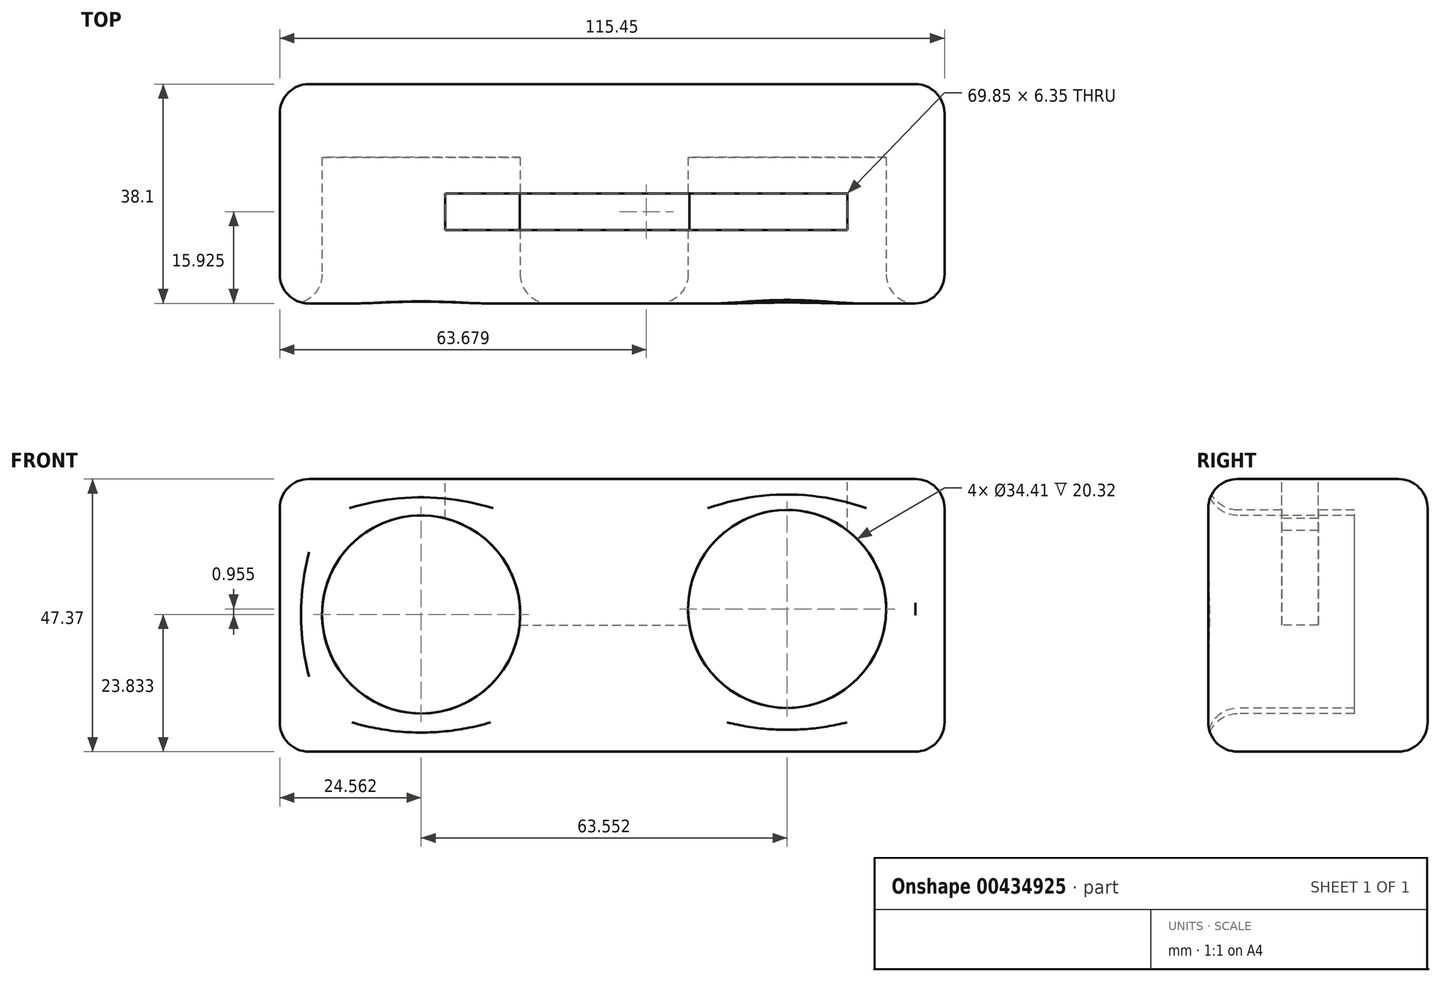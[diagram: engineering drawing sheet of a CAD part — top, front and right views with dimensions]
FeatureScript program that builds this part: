
annotation { "Feature Type Name" : "Feature", "Feature Type Description" : "" }
export const myFeature = defineFeature(function(context is Context, id is Id, definition is map)
    precondition{}
    {
        {
            var Q0;
            Q0=qCreatedBy(makeId("Front.planeOp"),FACE);
            var sketch = newSketch(context, id + "F0", { "sketchPlane" : qUnion([Q0])});
            skLineSegment(sketch, "E0.bottom", {"start": v(-65.78, 0) * mm, "end": v(68.72, 0) * mm});
            skLineSegment(sketch, "E0.top", {"start": v(-65.78, 47.37) * mm, "end": v(68.72, 47.37) * mm});
            skLineSegment(sketch, "E0.left", {"start": v(-65.78, 0) * mm, "end": v(-65.78, 47.37) * mm});
            skLineSegment(sketch, "E0.right", {"start": v(68.72, 0) * mm, "end": v(68.72, 47.37) * mm});
            skSolve(sketch);
        }
        {
            var Q0;
            Q0 = qSketchRegion(id + "F0", true);
            extrude(context, id + "F1", {"entities" : qUnion([Q0]), "depth" : 38.1 * mm});
        }
        {
            var Q0;
            Q0=makeQuery(id+"F1.opExtrude","CAP_FACE",FACE,{"disambiguationData":[OSD([sQuery(id+"F0.wireOp",EDGE,"E0.bottom"),sQuery(id+"F0.wireOp",EDGE,"E0.top"),sQuery(id+"F0.wireOp",EDGE,"E0.left"),sQuery(id+"F0.wireOp",EDGE,"E0.right")])],"isStart":false});
            var sketch = newSketch(context, id + "F2", { "sketchPlane" : qUnion([Q0])});
            skCircle(sketch, "E1", {"center": v(-41.22, 23.83) * mm, "radius": 17.2 * mm});
            skCircle(sketch, "E2", {"center": v(22.33, 24.79) * mm, "radius": 17.2 * mm});
            skSolve(sketch);
        }
        {
            var Q0;
            Q0 = qSketchRegion(id + "F2", true);
            extrude(context, id + "F3", {"entities" : qUnion([Q0]), "operationType" : NewBodyOperationType.REMOVE, "oppositeDirection" : true, "depth" : 25.4 * mm});
        }
        {
            var Q0;
            Q0=makeQuery(id+"F1.opExtrude","SWEPT_FACE",FACE,{"disambiguationData":[OSD([sQuery(id+"F0.wireOp",EDGE,"E0.top")])]});
            var sketch = newSketch(context, id + "F4", { "sketchPlane" : qUnion([Q0])});
            skLineSegment(sketch, "E3.bottom", {"start": v(-37.03, -19) * mm, "end": v(32.82, -19) * mm});
            skLineSegment(sketch, "E3.top", {"start": v(-37.03, -25.35) * mm, "end": v(32.82, -25.35) * mm});
            skLineSegment(sketch, "E3.left", {"start": v(-37.03, -19) * mm, "end": v(-37.03, -25.35) * mm});
            skLineSegment(sketch, "E3.right", {"start": v(32.82, -19) * mm, "end": v(32.82, -25.35) * mm});
            skSolve(sketch);
        }
        {
            var Q0;
            Q0=makeQuery(id+"F4.imprint","IMPRINT",FACE,{"disambiguationData":[TD([[makeQuery(id+"F4.imprint","IMPRINT",EDGE,{"derivedFrom":sQuery(id+"F4.wireOp",EDGE,"E3.bottom")}),-1.0]])]});
            extrude(context, id + "F5", {"entities" : qUnion([Q0]), "operationType" : NewBodyOperationType.REMOVE, "oppositeDirection" : true, "depth" : 25.4 * mm});
        }
        {
            var Q0;
            Q0=makeQuery(id+"F1.opExtrude","SWEPT_FACE",FACE,{"disambiguationData":[OSD([sQuery(id+"F0.wireOp",EDGE,"E0.right")])]});
            extrude(context, id + "F6", {"entities" : qUnion([Q0]), "operationType" : NewBodyOperationType.REMOVE, "oppositeDirection" : true, "depth" : 19.05 * mm});
        }
        {
            var Q0;
            Q0=makeQuery(id+"F1.opExtrude","CAP_EDGE",EDGE,{"disambiguationData":[OSD([sQuery(id+"F0.wireOp",EDGE,"E0.top")])],"isStart":false});
            var Q1;
            Q1=makeQuery(id+"F6.boolean.opBoolean","COPY",EDGE,{"derivedFrom":makeQuery(id+"F6.opExtrude","CAP_EDGE",EDGE,{"disambiguationData":[OSD([sQuery(id+"F0.wireOp",EDGE,"E0.top"),sQuery(id+"F0.wireOp",EDGE,"E0.right")])],"isStart":false})});
            var Q2;
            Q2=makeQuery(id+"F1.opExtrude","CAP_EDGE",EDGE,{"disambiguationData":[OSD([sQuery(id+"F0.wireOp",EDGE,"E0.top")])],"isStart":true});
            var Q3;
            Q3=makeQuery(id+"F1.opExtrude","SWEPT_EDGE",EDGE,{"disambiguationData":[OSD([sQuery(id+"F0.wireOp",EDGE,"E0.top"),sQuery(id+"F0.wireOp",EDGE,"E0.left")])]});
            var Q4;
            Q4=makeQuery(id+"F1.opExtrude","CAP_FACE",FACE,{"disambiguationData":[OSD([sQuery(id+"F0.wireOp",EDGE,"E0.bottom"),sQuery(id+"F0.wireOp",EDGE,"E0.top"),sQuery(id+"F0.wireOp",EDGE,"E0.left"),sQuery(id+"F0.wireOp",EDGE,"E0.right")])],"isStart":false});
            var Q5;
            Q5=makeQuery(id+"F6.boolean.opBoolean","COPY",FACE,{"derivedFrom":makeQuery(id+"F6.opExtrude","CAP_FACE",FACE,{"disambiguationData":[OSD([sQuery(id+"F0.wireOp",EDGE,"E0.right")])],"isStart":false})});
            var Q6;
            Q6=makeQuery(id+"F1.opExtrude","SWEPT_EDGE",EDGE,{"disambiguationData":[OSD([sQuery(id+"F0.wireOp",EDGE,"E0.bottom"),sQuery(id+"F0.wireOp",EDGE,"E0.left")])]});
            var Q7;
            Q7=makeQuery(id+"F1.opExtrude","CAP_EDGE",EDGE,{"disambiguationData":[OSD([sQuery(id+"F0.wireOp",EDGE,"E0.bottom")])],"isStart":true});
            var Q8;
            Q8=makeQuery(id+"F1.opExtrude","CAP_EDGE",EDGE,{"disambiguationData":[OSD([sQuery(id+"F0.wireOp",EDGE,"E0.left")])],"isStart":true});
            var Q9;
            Q9=makeQuery(id+"F5.boolean.opBoolean","COPY",EDGE,{"derivedFrom":makeQuery(id+"F5.opExtrude","CAP_EDGE",EDGE,{"disambiguationData":[OSD([sQuery(id+"F4.wireOp",EDGE,"E3.top")])],"isStart":true})});
            var Q10;
            Q10=makeQuery(id+"F5.boolean.opBoolean","COPY",EDGE,{"derivedFrom":makeQuery(id+"F5.opExtrude","CAP_EDGE",EDGE,{"disambiguationData":[OSD([sQuery(id+"F4.wireOp",EDGE,"E3.right")])],"isStart":true})});
            var Q11;
            Q11=makeQuery(id+"F5.boolean.opBoolean","COPY",EDGE,{"derivedFrom":makeQuery(id+"F5.opExtrude","CAP_EDGE",EDGE,{"disambiguationData":[OSD([sQuery(id+"F4.wireOp",EDGE,"E3.bottom")])],"isStart":true})});
            var Q12;
            Q12=makeQuery(id+"F5.boolean.opBoolean","COPY",EDGE,{"derivedFrom":makeQuery(id+"F5.opExtrude","CAP_EDGE",EDGE,{"disambiguationData":[OSD([sQuery(id+"F4.wireOp",EDGE,"E3.left")])],"isStart":true})});
            fillet(context, id + "F7", {"entities" : qUnion([Q0, Q1, Q2, Q3, Q4, Q5, Q6, Q7, Q8, Q9, Q10, Q11, Q12]), "radius" : 5.08 * mm, "tangentPropagation" : true, "allowEdgeOverflow" : false});
        }
    });
